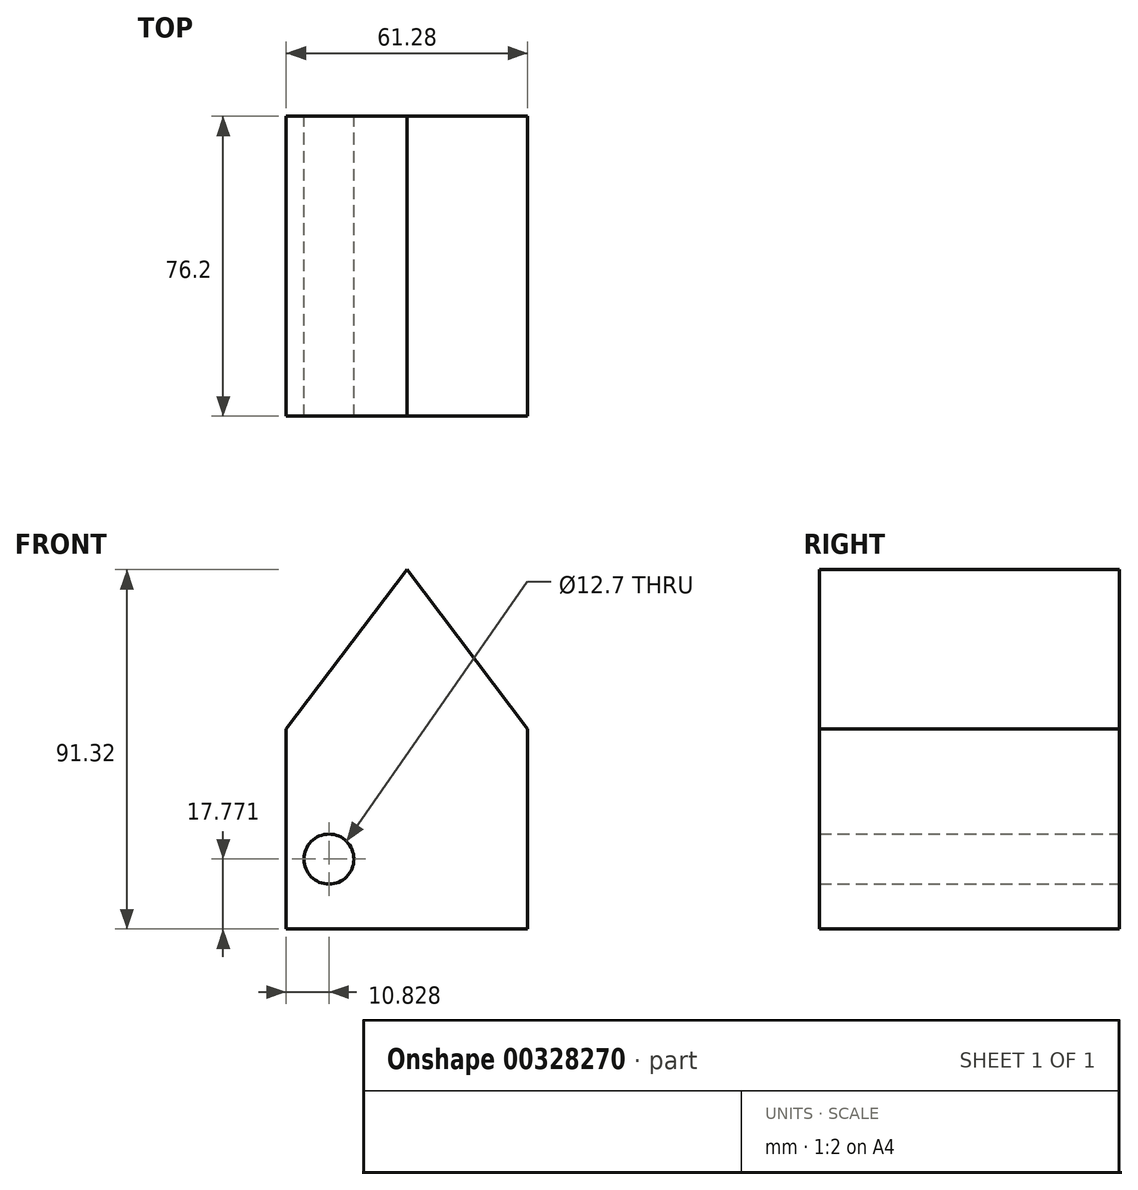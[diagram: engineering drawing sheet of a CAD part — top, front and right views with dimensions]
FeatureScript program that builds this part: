
annotation { "Feature Type Name" : "Feature", "Feature Type Description" : "" }
export const myFeature = defineFeature(function(context is Context, id is Id, definition is map)
    precondition{}
    {
        {
            var Q0;
            Q0=qCreatedBy(makeId("Front.planeOp"),FACE);
            var sketch = newSketch(context, id + "F0", { "sketchPlane" : qUnion([Q0])});
            skLineSegment(sketch, "E0.top", {"start": v(-30.64, -25.4) * mm, "end": v(30.64, -25.4) * mm});
            skLineSegment(sketch, "E0.left", {"start": v(-30.64, 25.4) * mm, "end": v(-30.64, -25.4) * mm});
            skLineSegment(sketch, "E0.right", {"start": v(30.64, 25.4) * mm, "end": v(30.64, -25.4) * mm});
            skPoint(sketch, "E0.middle", {"position": v(0, 0) * mm});
            skLineSegment(sketch, "E1", {"start": v(-30.64, 25.4) * mm, "end": v(0, 65.92) * mm});
            skLineSegment(sketch, "E2", {"start": v(0, 65.92) * mm, "end": v(30.64, 25.4) * mm});
            skCircle(sketch, "E3", {"center": v(-19.81, -7.63) * mm, "radius": 6.35 * mm});
            skSolve(sketch);
        }
        {
            var Q0;
            Q0=makeQuery(id+"F0.imprint","IMPRINT",FACE,{"disambiguationData":[TD([[makeQuery(id+"F0.imprint","IMPRINT",EDGE,{"derivedFrom":sQuery(id+"F0.wireOp",EDGE,"E0.top")}),1.0]])]});
            extrude(context, id + "F1", {"entities" : qUnion([Q0]), "depth" : 76.2 * mm});
        }
    });
